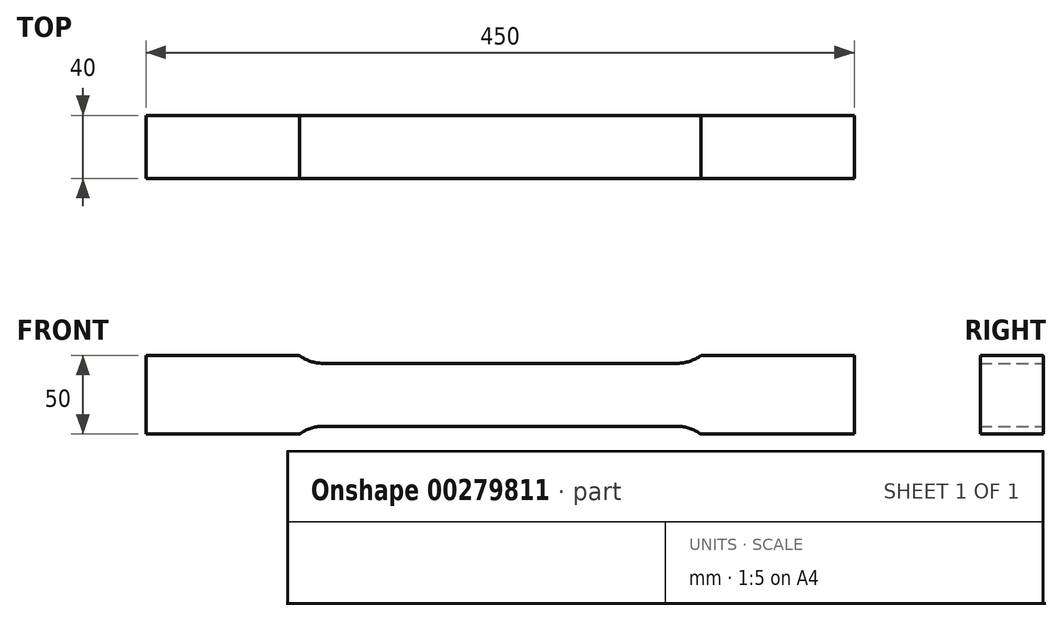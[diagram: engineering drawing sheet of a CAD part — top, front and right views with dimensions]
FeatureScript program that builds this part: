
annotation { "Feature Type Name" : "Feature", "Feature Type Description" : "" }
export const myFeature = defineFeature(function(context is Context, id is Id, definition is map)
    precondition{}
    {
        {
            var Q0;
            Q0=qCreatedBy(makeId("Front.planeOp"),FACE);
            var sketch = newSketch(context, id + "F0", { "sketchPlane" : qUnion([Q0])});
            skLineSegment(sketch, "E0", {"start": v(0, 20) * mm, "end": v(112.5, 20) * mm});
            skArc(sketch, "E1", {"start": v(112.5, 20) * mm, "mid": v(120.4, 21.28) * mm, "end": v(127.5, 25) * mm});
            skLineSegment(sketch, "E2", {"start": v(127.5, 25) * mm, "end": v(225, 25) * mm});
            skLineSegment(sketch, "E3", {"start": v(225, 25) * mm, "end": v(225, 0) * mm});
            skLineSegment(sketch, "E4.MirrorCS", {"start": v(0, -20) * mm, "end": v(112.5, -20) * mm});
            skLineSegment(sketch, "E5.MirrorCS", {"start": v(225, -25) * mm, "end": v(225, 0) * mm});
            skLineSegment(sketch, "E6.MirrorCS", {"start": v(127.5, -25) * mm, "end": v(225, -25) * mm});
            skArc(sketch, "E7.MirrorCS", {"start": v(112.5, -20) * mm, "mid": v(120.4, -21.28) * mm, "end": v(127.5, -25) * mm});
            skArc(sketch, "E8.MirrorCS", {"start": v(-112.5, -20) * mm, "mid": v(-120.4, -21.28) * mm, "end": v(-127.5, -25) * mm});
            skLineSegment(sketch, "E9.MirrorCS", {"start": v(-127.5, -25) * mm, "end": v(-225, -25) * mm});
            skArc(sketch, "E10.MirrorCS", {"start": v(-112.5, 20) * mm, "mid": v(-120.4, 21.28) * mm, "end": v(-127.5, 25) * mm});
            skLineSegment(sketch, "E11.MirrorCS", {"start": v(-127.5, 25) * mm, "end": v(-225, 25) * mm});
            skLineSegment(sketch, "E12.MirrorCS", {"start": v(-225, -25) * mm, "end": v(-225, 0) * mm});
            skLineSegment(sketch, "E13.MirrorCS", {"start": v(0, 20) * mm, "end": v(-112.5, 20) * mm});
            skLineSegment(sketch, "E14.MirrorCS", {"start": v(-225, 25) * mm, "end": v(-225, 0) * mm});
            skLineSegment(sketch, "E15.MirrorCS", {"start": v(0, -20) * mm, "end": v(-112.5, -20) * mm});
            skSolve(sketch);
        }
        {
            var Q0;
            Q0=makeQuery(id+"F0.imprint","IMPRINT",FACE,{"disambiguationData":[TD([[makeQuery(id+"F0.imprint","IMPRINT",EDGE,{"derivedFrom":sQuery(id+"F0.wireOp",EDGE,"E0")}),-1.0]])]});
            extrude(context, id + "F1", {"entities" : qUnion([Q0]), "endBound" : BoundingType.SYMMETRIC, "depth" : 40 * mm});
        }
    });
